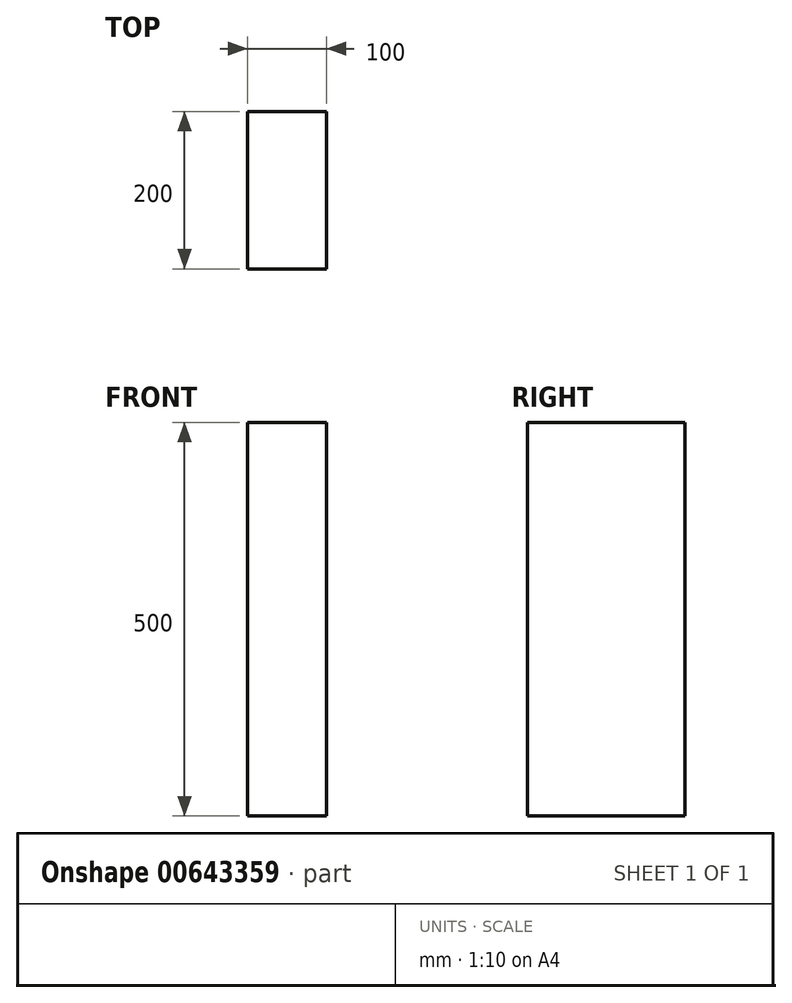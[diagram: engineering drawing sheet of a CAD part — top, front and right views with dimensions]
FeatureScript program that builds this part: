
annotation { "Feature Type Name" : "Feature", "Feature Type Description" : "" }
export const myFeature = defineFeature(function(context is Context, id is Id, definition is map)
    precondition{}
    {
        {
            var Q0;
            Q0=qCreatedBy(makeId("Top.planeOp"),FACE);
            var sketch = newSketch(context, id + "F0", { "sketchPlane" : qUnion([Q0])});
            skLineSegment(sketch, "E0.bottom", {"start": v(-127.97, 170.95) * mm, "end": v(-27.97, 170.95) * mm});
            skLineSegment(sketch, "E0.top", {"start": v(-127.97, -29.05) * mm, "end": v(-27.97, -29.05) * mm});
            skLineSegment(sketch, "E0.left", {"start": v(-127.97, 170.95) * mm, "end": v(-127.97, -29.05) * mm, "construction": true});
            skLineSegment(sketch, "E0.right", {"start": v(-27.97, 170.95) * mm, "end": v(-27.97, -29.05) * mm});
            skLineSegment(sketch, "E1", {"start": v(-127.97, -29.05) * mm, "end": v(-127.97, 170.95) * mm});
            skSolve(sketch);
        }
        {
            var Q0;
            Q0 = qSketchRegion(id + "F0", true);
            extrude(context, id + "F1", {"entities" : qUnion([Q0]), "depth" : 500 * mm, "offsetDistance" : 25 * mm});
        }
    });
